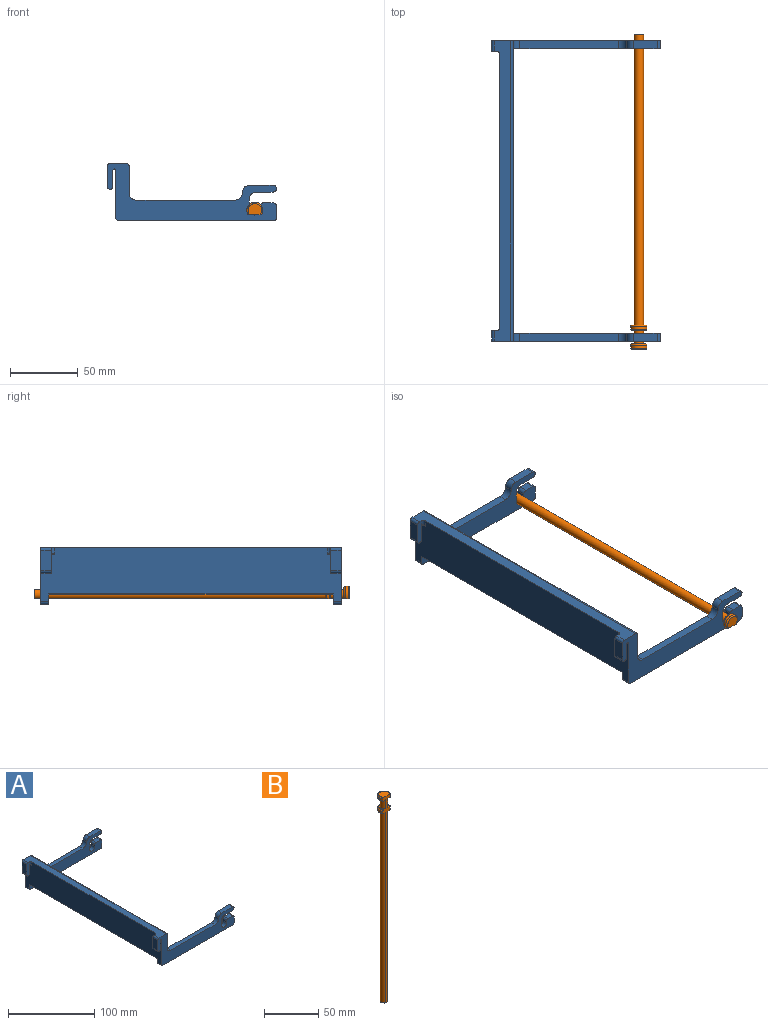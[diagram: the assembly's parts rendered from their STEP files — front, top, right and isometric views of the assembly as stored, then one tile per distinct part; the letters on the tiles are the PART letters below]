
ASSEMBLY  parts=2 mates=1
PART A: 59 faces, bbox 124.8x222x42 mm
  f0: plane 15x8mm, normal (-1,0,0), area 120mm2, adj f1,f4,f32,f55
  f1: cylinder r=2mm len=8mm, axis (0,1,0), area 50.3mm2, adj f0,f2,f32,f55
  f2: plane 12x8mm, normal (1,0,0), area 96mm2, adj f1,f3,f32,f55
  f3: cylinder r=1mm len=10mm, axis (0,1,0), area 26.8mm2, adj f2,f9,f32,f57
  f4: cylinder r=2mm len=8mm, axis (0,1,0), area 25.1mm2, adj f0,f30,f32,f55
  f5: plane 15x8mm, normal (-1,0,0), area 120mm2, adj f6,f31,f53,f56
  f6: cylinder r=2mm len=8mm, axis (0,1,0), area 50.3mm2, adj f5,f7,f53,f56
  f7: plane 12x8mm, normal (1,0,0), area 96mm2, adj f6,f8,f53,f56
  f8: cylinder r=1mm len=10mm, axis (0,1,0), area 26.8mm2, adj f7,f9,f53,f58
  f9: plane 222x40mm, normal (-1,0,0), area 7570.2mm2, adj f3,f8,f10,f30,f32,f33,f34,f35
  f10: cylinder r=2mm len=6mm, axis (0,1,0), area 18.8mm2, adj f9,f11,f32,f33
  f11: plane 114.81x6mm, normal (0,0,-1), area 688.9mm2, adj f10,f12,f32,f33
  f12: cylinder r=2mm len=6mm, axis (0,1,0), area 18.8mm2, adj f11,f13,f32,f33
  f13: plane 8.5x6mm, normal (1,0,0), area 51mm2, adj f12,f14,f32,f33
  f14: cylinder r=2.5mm len=6mm, axis (0,1,0), area 23.6mm2, adj f13,f15,f32,f33
  f15: plane 7x6mm, normal (0,0,1), area 42mm2, adj f14,f16,f32,f33
  f16: cylinder r=2.5mm len=6mm, axis (0,1,0), area 23.6mm2, adj f15,f17,f32,f33
  f17: plane 6x2.5mm, normal (-1,0,0), area 15mm2, adj f16,f18,f32,f33
  f18: cylinder r=4mm len=8mm, axis (0,1,0), area 75.4mm2, adj f17,f19,f32,f33
  f19: plane 8x6mm, normal (1,0,0), area 48mm2, adj f18,f20,f32,f33
  f20: cylinder r=5mm len=6mm, axis (0,1,0), area 47.1mm2, adj f19,f21,f32,f33
  f21: plane 12.5x6mm, normal (0,0,-1), area 75mm2, adj f20,f22,f32,f33
  f22: cylinder r=2.5mm len=6mm, axis (0,1,0), area 47.1mm2, adj f21,f23,f32,f33
  f23: plane 17.5x6mm, normal (0,0,1), area 105mm2, adj f22,f24,f32,f33
  f24: cylinder r=5mm len=6mm, axis (0,1,0), area 47.1mm2, adj f23,f25,f32,f33
  f25: cylinder r=6mm len=6mm, axis (0,1,0), area 56.5mm2, adj f24,f26,f32,f33
  f26: plane 72.81x6mm, normal (0,0,1), area 436.9mm2, adj f25,f27,f32,f33
  f27: cylinder r=5mm len=6mm, axis (0,1,0), area 47.1mm2, adj f26,f28,f32,f33
  f28: plane 222x24.49mm, normal (1,0,0), area 5383.6mm2, adj f27,f29,f32,f33,f34,f52,f53,f54
  f29: cylinder r=2mm len=222mm, axis (0,1,0), area 697.4mm2, adj f28,f30,f32,f53
  f30: plane 222x12mm, normal (0,0,1), area 1841.7mm2, adj f4,f9,f29,f31,f32,f53,f55,f56
  f31: cylinder r=2mm len=8mm, axis (0,1,0), area 25.1mm2, adj f5,f30,f53,f56
  f32: plane 124.81x42mm, normal (0,-1,0), area 2189mm2, adj f0,f1,f2,f3,f4,f9,f10,f11
  f33: plane 118.81x26mm, normal (0,1,0), area 1777mm2, adj f9,f10,f11,f12,f13,f14,f15,f16
  f34: cylinder r=8mm len=210mm, axis (0,-1,0), area 3063.4mm2, adj f9,f28,f33,f54
  f35: cylinder r=2mm len=6mm, axis (0,-1,0), area 18.8mm2, adj f9,f36,f53,f54
  f36: plane 114.81x6mm, normal (0,0,-1), area 688.9mm2, adj f35,f37,f53,f54
  f37: cylinder r=2mm len=6mm, axis (0,-1,0), area 18.8mm2, adj f36,f38,f53,f54
  f38: plane 8.5x6mm, normal (1,0,0), area 51mm2, adj f37,f39,f53,f54
  f39: cylinder r=2.5mm len=6mm, axis (0,-1,0), area 23.6mm2, adj f38,f40,f53,f54
  f40: plane 7x6mm, normal (0,0,1), area 42mm2, adj f39,f41,f53,f54
  f41: cylinder r=2.5mm len=6mm, axis (0,-1,0), area 23.6mm2, adj f40,f42,f53,f54
  f42: plane 6x2.5mm, normal (-1,0,0), area 15mm2, adj f41,f43,f53,f54
  f43: cylinder r=4mm len=8mm, axis (0,-1,0), area 75.4mm2, adj f42,f44,f53,f54
  f44: plane 8x6mm, normal (1,0,0), area 48mm2, adj f43,f45,f53,f54
  f45: cylinder r=5mm len=6mm, axis (0,-1,0), area 47.1mm2, adj f44,f46,f53,f54
  f46: plane 12.5x6mm, normal (0,0,-1), area 75mm2, adj f45,f47,f53,f54
  f47: cylinder r=2.5mm len=6mm, axis (0,-1,0), area 47.1mm2, adj f46,f48,f53,f54
  f48: plane 17.5x6mm, normal (0,0,1), area 105mm2, adj f47,f49,f53,f54
  f49: cylinder r=5mm len=6mm, axis (0,-1,0), area 47.1mm2, adj f48,f50,f53,f54
  f50: cylinder r=6mm len=6mm, axis (0,-1,0), area 56.5mm2, adj f49,f51,f53,f54
  f51: plane 72.81x6mm, normal (0,0,1), area 436.9mm2, adj f50,f52,f53,f54
  f52: cylinder r=5mm len=6mm, axis (0,-1,0), area 47.1mm2, adj f28,f51,f53,f54
  f53: plane 124.81x42mm, normal (0,1,0), area 2189mm2, adj f5,f6,f7,f8,f9,f28,f29,f30
  f54: plane 118.81x26mm, normal (0,-1,0), area 1777mm2, adj f9,f28,f34,f35,f36,f37,f38,f39
  f55: plane 19x4mm, normal (0,1,0), area 73.4mm2, adj f0,f1,f2,f4,f30,f57
  f56: plane 19x4mm, normal (0,-1,0), area 73.4mm2, adj f5,f6,f7,f30,f31,f58
  f57: cylinder r=2mm len=5mm, axis (0,0,-1), area 13.6mm2, adj f3,f9,f30,f55
  f58: cylinder r=2mm len=5mm, axis (0,0,1), area 13.6mm2, adj f8,f9,f30,f56
PART B: 14 faces, bbox 13x10.7x232.5 mm
  f0: cylinder r=3.5mm len=10mm, axis (0,0,-1), area 190.7mm2, adj f5,f6,f13
  f1: cylinder r=3.5mm len=214.5mm, axis (0,0,-1), area 4090.9mm2, adj f2,f3,f13
  f2: plane 7x6.7mm, normal (0,0,-1), area 37.9mm2, adj f1,f13
  f3: plane 10x8.2mm, normal (0,0,-1), area 31mm2, adj f1,f11,f13
  f4: cylinder r=6mm len=12mm, axis (0,0,-1), area 51.2mm2, adj f11,f12,f13
  f5: plane 10x8.2mm, normal (0,0,1), area 31mm2, adj f0,f12,f13
  f6: plane 10x8.2mm, normal (0,0,-1), area 31mm2, adj f0,f9,f13
  f7: cylinder r=6mm len=12mm, axis (0,0,-1), area 51.2mm2, adj f9,f10,f13
  f8: plane 10x8.2mm, normal (0,0,1), area 68.9mm2, adj f10,f13
  f9: torus R=5mm, axis (0,0,1), area 38.5mm2, adj f6,f7,f13
  f10: torus R=5mm, axis (0,0,1), area 38.5mm2, adj f7,f8,f13
  f11: torus R=5mm, axis (0,0,-1), area 38.5mm2, adj f3,f4,f13
  f12: torus R=5mm, axis (0,0,-1), area 38.5mm2, adj f4,f5,f13
  f13: plane 232.5x10.15mm, normal (0,-1,0), area 715.7mm2, adj f0,f1,f2,f3,f4,f5,f6,f7
PLACE A t=(19.46,-100.85,27.03)mm
PLACE B rot(axis=(1,0,0),90deg) t=(19.46,4.15,19.48)mm
MATE planar B.f8 <-> A.f18  axis (0,-1,0) through (19.46,-112.85,20.03)mm
